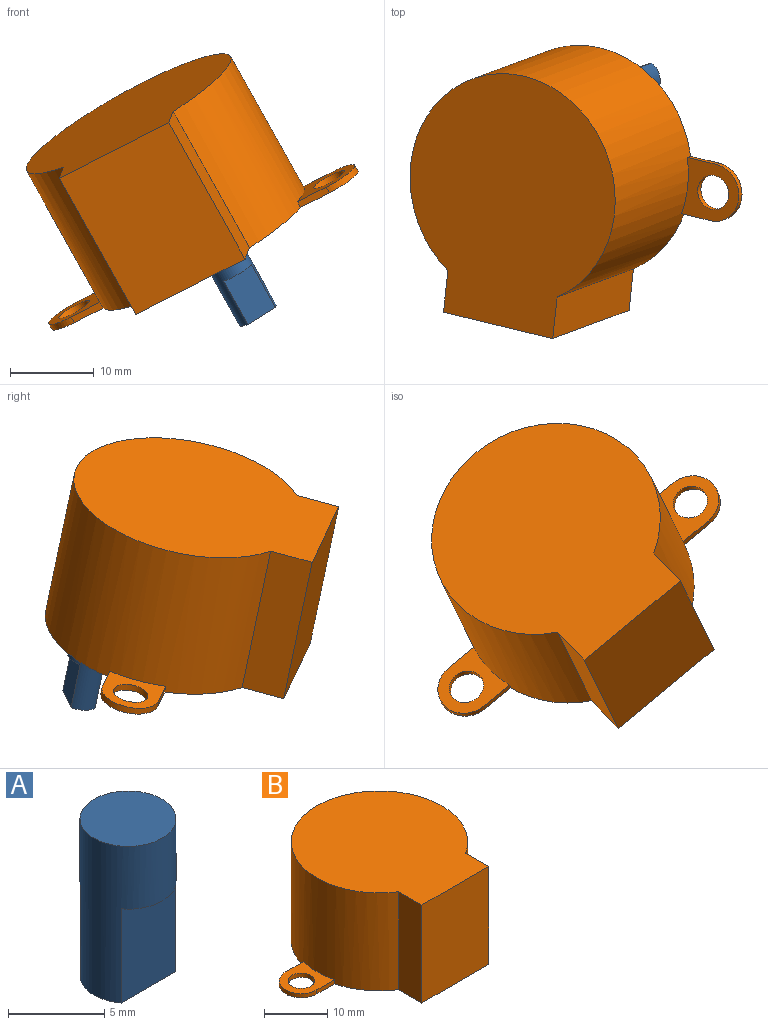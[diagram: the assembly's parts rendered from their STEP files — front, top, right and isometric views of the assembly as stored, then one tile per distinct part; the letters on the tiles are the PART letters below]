
ASSEMBLY  parts=2 mates=1
PART A: 7 faces, bbox 5x5x10 mm
  f0: plane 5x3mm, normal (0,0,-1), area 14mm2, adj f1,f3,f5
  f1: cylinder r=2.5mm len=10mm, axis (0,0,1), area 101.4mm2, adj f0,f2,f3,f4,f5,f6
  f2: plane 5x5mm, normal (0,0,1), area 19.6mm2, adj f1
  f3: plane 6x4mm, normal (0,1,0), area 24mm2, adj f0,f1,f4
  f4: plane 4x1mm, normal (0,0,-1), area 2.8mm2, adj f1,f3
  f5: plane 6x4mm, normal (0,-1,0), area 24mm2, adj f0,f1,f6
  f6: plane 4x1mm, normal (0,0,-1), area 2.8mm2, adj f1,f5
PART B: 20 faces, bbox 42x31x20.5 mm
  f0: cylinder r=14mm len=28mm, axis (0,0,-1), area 1359.2mm2, adj f2,f3,f4,f5,f6,f7,f10,f11
  f1: plane 19x15mm, normal (0,-1,0), area 285mm2, adj f2,f3,f4,f5
  f2: plane 19x5.18mm, normal (1,0,0), area 98.4mm2, adj f0,f1,f4,f5
  f3: plane 19x5.18mm, normal (-1,0,0), area 98.4mm2, adj f0,f1,f4,f5
  f4: plane 31x28mm, normal (0,0,1), area 671.3mm2, adj f0,f1,f2,f3
  f5: plane 42x31mm, normal (0,0,-1), area 669.5mm2, adj f0,f1,f2,f3,f6,f7,f8,f9
  f6: plane 3.94x0.8mm, normal (0,1,0), area 3.2mm2, adj f0,f5,f9,f10
  f7: plane 3.94x0.8mm, normal (0,-1,0), area 3.2mm2, adj f0,f5,f9,f10
  f8: cylinder r=2.1mm len=4.2mm, axis (0,0,-1), area 10.6mm2, adj f5,f10
  f9: cylinder r=3.5mm len=7mm, axis (0,0,-1), area 8.8mm2, adj f5,f6,f7,f10
  f10: plane 7.44x7mm, normal (0,0,1), area 30.9mm2, adj f0,f6,f7,f8,f9
  f11: plane 3.94x0.8mm, normal (0,-1,0), area 3.2mm2, adj f0,f5,f14,f15
  f12: plane 3.94x0.8mm, normal (0,1,0), area 3.2mm2, adj f0,f5,f14,f15
  f13: cylinder r=2.1mm len=4.2mm, axis (0,0,-1), area 10.6mm2, adj f5,f15
  f14: cylinder r=3.5mm len=7mm, axis (0,0,-1), area 8.8mm2, adj f5,f11,f12,f15
  f15: plane 7.44x7mm, normal (0,0,1), area 30.9mm2, adj f0,f11,f12,f13,f14
  f16: cylinder r=2.5mm len=5mm, axis (0,0,1), area 23.6mm2, adj f18,f19
  f17: cylinder r=4.5mm len=9mm, axis (0,0,1), area 42.4mm2, adj f5,f18
  f18: plane 9x9mm, normal (0,0,-1), area 44mm2, adj f16,f17
  f19: plane 5x5mm, normal (0,0,-1), area 19.6mm2, adj f16
PLACE A rot(axis=(0.18,-0.86,0.48),35.3deg) t=(7.71,0.57,-1.81)mm
PLACE B rot(axis=(0.41,-0.86,-0.29),32.3deg) t=(3.74,0.23,-2.36)mm
MATE revolute A.f1 <-> B.f16  axis (-0.48,-0.18,0.86) through (5.28,8.19,-1.58)mm
